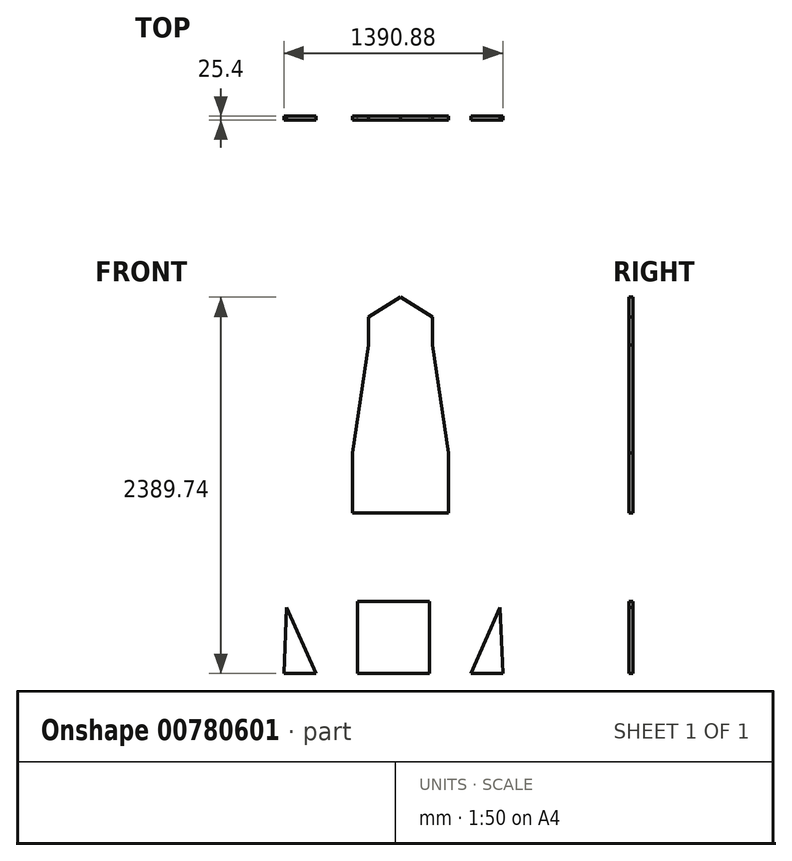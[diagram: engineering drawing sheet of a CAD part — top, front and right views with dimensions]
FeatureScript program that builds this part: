
annotation { "Feature Type Name" : "Feature", "Feature Type Description" : "" }
export const myFeature = defineFeature(function(context is Context, id is Id, definition is map)
    precondition{}
    {
        {
            var Q0;
            Q0=qCreatedBy(makeId("Front.planeOp"),FACE);
            var sketch = newSketch(context, id + "F0", { "sketchPlane" : qUnion([Q0])});
            skLineSegment(sketch, "E0.bottom", {"start": v(-302, 266.87) * mm, "end": v(155.2, 266.87) * mm});
            skLineSegment(sketch, "E0.top", {"start": v(-302, -190.33) * mm, "end": v(155.2, -190.33) * mm});
            skLineSegment(sketch, "E0.left", {"start": v(-302, 266.87) * mm, "end": v(-302, -190.33) * mm});
            skLineSegment(sketch, "E0.right", {"start": v(155.2, 266.87) * mm, "end": v(155.2, -190.33) * mm});
            skPoint(sketch, "E1.startSnap0", {"position": v(-73.4, 266.87) * mm});
            skLineSegment(sketch, "E2.MirrorCS", {"start": v(-565.64, -190.33) * mm, "end": v(-751.33, 227.46) * mm});
            skLineSegment(sketch, "E3.MirrorCS", {"start": v(-768.84, -190.33) * mm, "end": v(-751.33, 227.46) * mm});
            skLineSegment(sketch, "E4.MirrorCS", {"start": v(-565.64, -190.33) * mm, "end": v(-768.84, -190.33) * mm});
            skLineSegment(sketch, "E5.MirrorCS", {"start": v(418.84, -190.33) * mm, "end": v(604.52, 227.46) * mm});
            skLineSegment(sketch, "E6.MirrorCS", {"start": v(622.04, -190.33) * mm, "end": v(604.52, 227.46) * mm});
            skLineSegment(sketch, "E7.MirrorCS", {"start": v(418.84, -190.33) * mm, "end": v(622.04, -190.33) * mm});
            skLineSegment(sketch, "E8", {"start": v(276.54, 827.8) * mm, "end": v(-333.06, 827.81) * mm});
            skLineSegment(sketch, "E9", {"start": v(276.54, 827.8) * mm, "end": v(276.54, 1208.8) * mm});
            skLineSegment(sketch, "E10", {"start": v(276.54, 1208.8) * mm, "end": v(174.94, 1894.6) * mm});
            skLineSegment(sketch, "E11.MirrorCS", {"start": v(-333.06, 1208.8) * mm, "end": v(-231.46, 1894.6) * mm});
            skLineSegment(sketch, "E12.MirrorCS", {"start": v(-333.06, 827.8) * mm, "end": v(-333.06, 1208.8) * mm});
            skLineSegment(sketch, "E13", {"start": v(-28.26, 2199.4) * mm, "end": v(174.94, 2072.4) * mm});
            skLineSegment(sketch, "E14", {"start": v(-231.46, 2072.4) * mm, "end": v(-231.46, 1894.6) * mm});
            skLineSegment(sketch, "E15", {"start": v(174.94, 2072.4) * mm, "end": v(174.94, 1894.6) * mm});
            skLineSegment(sketch, "E16", {"start": v(-231.46, 2072.4) * mm, "end": v(-28.26, 2199.4) * mm});
            skLineSegment(sketch, "E17", {"start": v(-231.46, 1894.6) * mm, "end": v(174.94, 1894.6) * mm, "construction": true});
            skLineSegment(sketch, "E18", {"start": v(-333.06, 1208.8) * mm, "end": v(-231.46, 1208.8) * mm, "construction": true});
            skLineSegment(sketch, "E19", {"start": v(276.54, 1208.8) * mm, "end": v(174.94, 1208.8) * mm, "construction": true});
            skLineSegment(sketch, "E20", {"start": v(-231.46, 1208.8) * mm, "end": v(-231.46, 1005.6) * mm, "construction": true});
            skLineSegment(sketch, "E21", {"start": v(174.94, 1208.8) * mm, "end": v(174.94, 1005.6) * mm, "construction": true});
            skLineSegment(sketch, "E22", {"start": v(-231.46, 1005.6) * mm, "end": v(174.94, 1005.6) * mm, "construction": true});
            skLineSegment(sketch, "E23", {"start": v(-231.46, 1208.8) * mm, "end": v(174.94, 1208.8) * mm, "construction": true});
            skLineSegment(sketch, "E24", {"start": v(-231.46, 979.87) * mm, "end": v(-79.06, 979.88) * mm, "construction": true});
            skLineSegment(sketch, "E25", {"start": v(-260.88, 1116.6) * mm, "end": v(-260.88, 1005.6) * mm, "construction": true});
            skLineSegment(sketch, "E26", {"start": v(-28.26, 1208.8) * mm, "end": v(-28.26, 1894.6) * mm});
            skPoint(sketch, "E26.endSnap0", {"position": v(-28.26, 1894.6) * mm});
            skSolve(sketch);
        }
        {
            var Q0;
            Q0=qSketchRegion(id+"F0",true);
            extrude(context, id + "F1", {"entities" : qUnion([Q0]), "depth" : 25.4 * mm, "offsetDistance" : 25.4 * mm});
        }
    });
